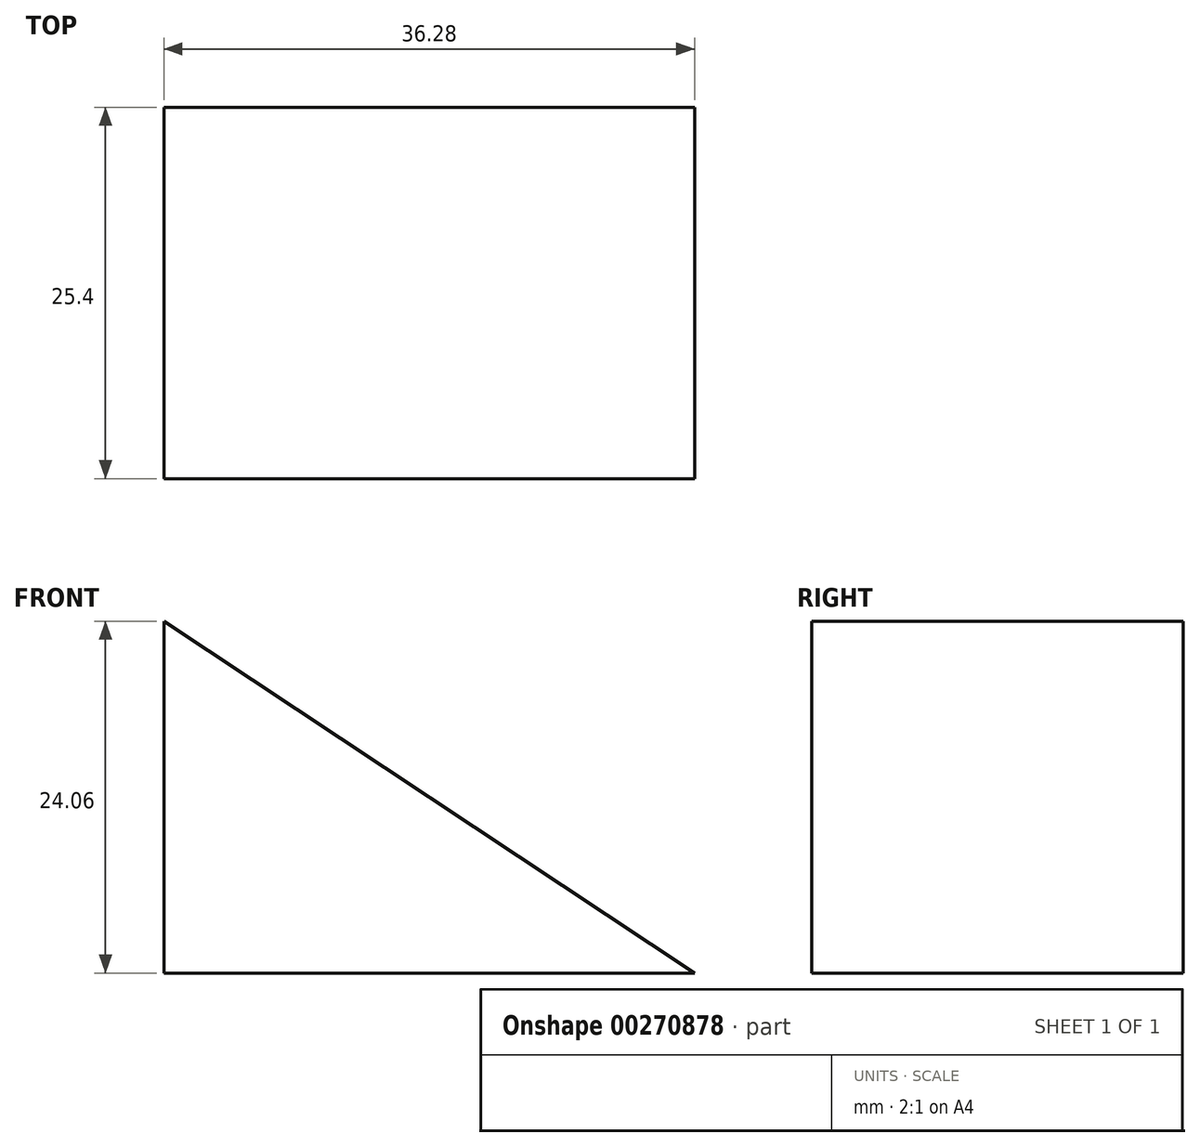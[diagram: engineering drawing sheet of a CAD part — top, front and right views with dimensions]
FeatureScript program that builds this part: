
annotation { "Feature Type Name" : "Feature", "Feature Type Description" : "" }
export const myFeature = defineFeature(function(context is Context, id is Id, definition is map)
    precondition{}
    {
        {
            var Q0;
            Q0=qCreatedBy(makeId("Front.planeOp"),FACE);
            var sketch = newSketch(context, id + "F0", { "sketchPlane" : qUnion([Q0])});
            skLineSegment(sketch, "E0", {"start": v(0, 0) * mm, "end": v(-36.28, 24.06) * mm});
            skLineSegment(sketch, "E1", {"start": v(-36.28, 24.06) * mm, "end": v(-36.28, 0) * mm});
            skLineSegment(sketch, "E2", {"start": v(-36.28, 0) * mm, "end": v(0, 0) * mm});
            skSolve(sketch);
        }
        {
            var Q0;
            Q0 = qSketchRegion(id + "F0", true);
            extrude(context, id + "F1", {"entities" : qUnion([Q0]), "depth" : 25.4 * mm});
        }
    });
